# Revit family: Sanitary_Showers_hansgrohe_28048XXX-Activera-Select-S-Shower-set-95_2jet_EcoSmart_shower-bar-Varia-72
name_source: partatom
category: Plumbing Fixtures
units: mm (PartAtom-declared; Revit-internal decimal feet)

## family parameters
Cut with Voids When Loaded = Yes
Host = Face
Maintain Annotation Orientation = No
OmniClass Number = 23.31.17.00
OmniClass Title = Showers
Part Type = Normal
Room Calculation Point = No
Round Connector Dimension = Use Diameter
Shared = No

## types (2) — shared parameters
Description = Activera Select S Shower set 95 2jet EcoSmart with shower bar Varia 72 cm
Manufacturer = Hansgrohe
Model = 28048XXX
Product Page URL = https://www.hansgrohe.com
Product data url = https://www.bimobject.com
URL = https://www.hansgrohe.com
Version = 1
zero-valued in all types: Default Elevation

## per-type parameters (varying)
| type | Material 1 |
| 000 Chrome | Hansgrohe - Metal - 000 Chrome |
| 670 Matte Black | Hansgrohe - Metal - 670 Matte Black |

## geometry (parser evidence)
native form markers: Sweep x2
no freeform markers — native parametric forms only
